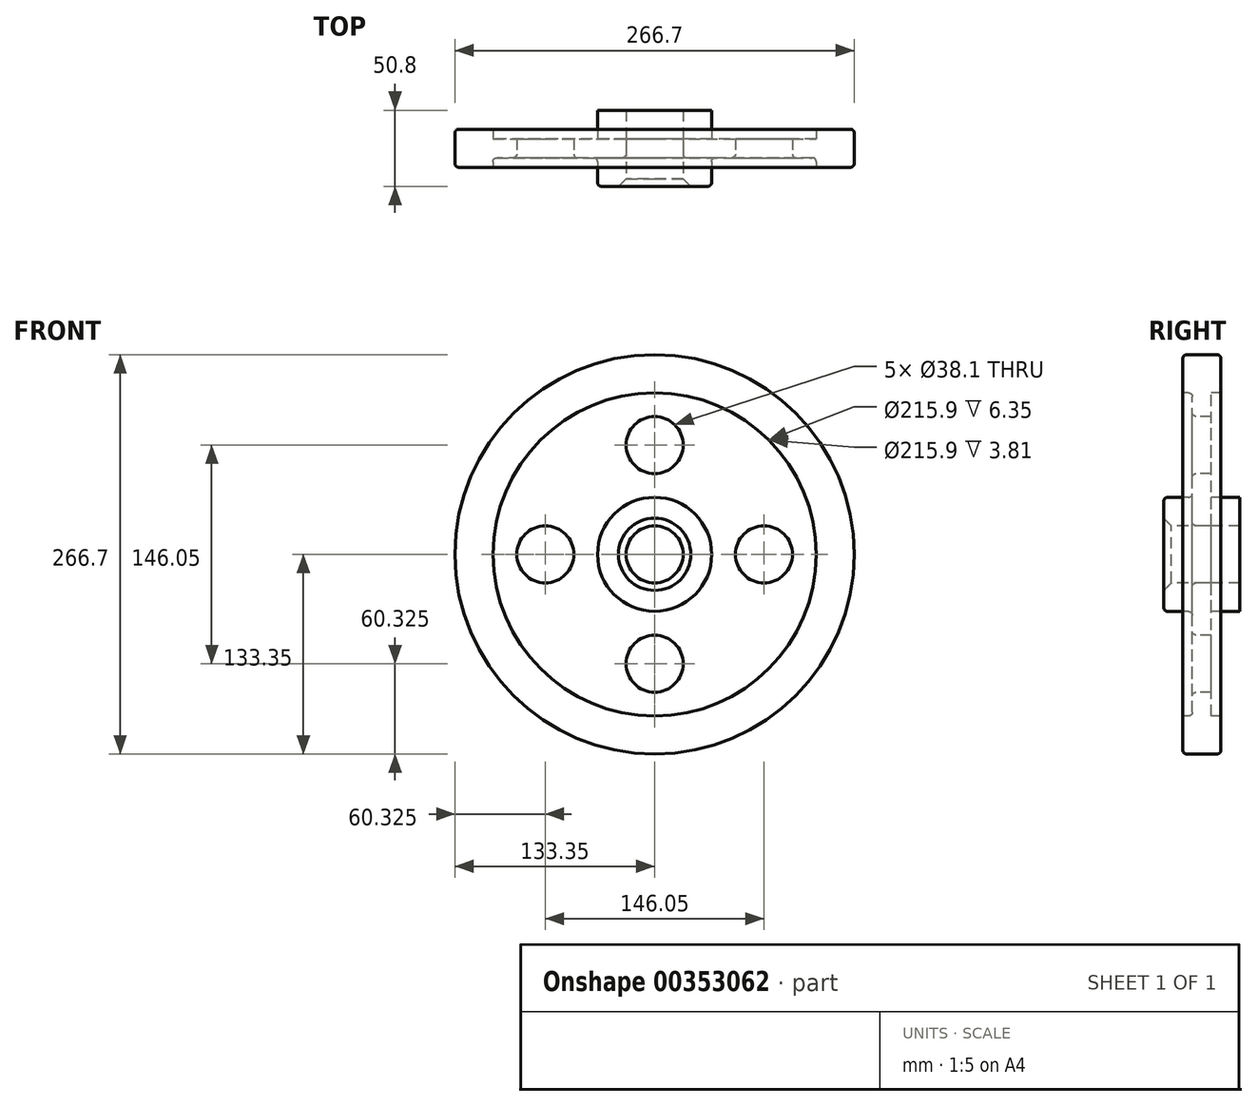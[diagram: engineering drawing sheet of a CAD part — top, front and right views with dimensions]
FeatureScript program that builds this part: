
annotation { "Feature Type Name" : "Feature", "Feature Type Description" : "" }
export const myFeature = defineFeature(function(context is Context, id is Id, definition is map)
    precondition{}
    {
        {
            var Q0;
            Q0=qCreatedBy(makeId("Right.planeOp"),FACE);
            var sketch = newSketch(context, id + "F0", { "sketchPlane" : qUnion([Q0])});
            skLineSegment(sketch, "E0", {"start": v(0, 0) * mm, "end": v(216.84, 0) * mm, "construction": true});
            skLineSegment(sketch, "E1", {"start": v(0, 0) * mm, "end": v(0, 371.48) * mm, "construction": true});
            skLineSegment(sketch, "E2.0", {"start": v(6.35, 38.1) * mm, "end": v(6.35, 107.95) * mm});
            skLineSegment(sketch, "E3.0", {"start": v(25.4, 19.05) * mm, "end": v(25.4, 38.1) * mm});
            skLineSegment(sketch, "E4.0", {"start": v(0, 19.05) * mm, "end": v(25.4, 19.05) * mm});
            skLineSegment(sketch, "E5.0", {"start": v(6.35, 38.1) * mm, "end": v(25.4, 38.1) * mm});
            skLineSegment(sketch, "E6.0", {"start": v(6.35, 107.95) * mm, "end": v(12.7, 107.95) * mm});
            skLineSegment(sketch, "E7.0", {"start": v(0, 133.35) * mm, "end": v(12.7, 133.35) * mm});
            skLineSegment(sketch, "E8.trimOffspring", {"start": v(12.7, 107.95) * mm, "end": v(12.7, 133.35) * mm});
            skLineSegment(sketch, "E9.MirrorCS", {"start": v(0, 133.35) * mm, "end": v(-12.7, 133.35) * mm});
            skLineSegment(sketch, "E10.MirrorCS", {"start": v(-12.7, 107.95) * mm, "end": v(-12.7, 133.35) * mm});
            skLineSegment(sketch, "E11.MirrorCS", {"start": v(-6.35, 38.1) * mm, "end": v(-6.35, 107.95) * mm});
            skLineSegment(sketch, "E12.MirrorCS", {"start": v(-6.35, 107.95) * mm, "end": v(-12.7, 107.95) * mm});
            skLineSegment(sketch, "E13.MirrorCS", {"start": v(-6.35, 38.1) * mm, "end": v(-25.4, 38.1) * mm});
            skLineSegment(sketch, "E14.MirrorCS", {"start": v(-25.4, 19.05) * mm, "end": v(-25.4, 38.1) * mm});
            skLineSegment(sketch, "E15.MirrorCS", {"start": v(0, 19.05) * mm, "end": v(-25.4, 19.05) * mm});
            skLineSegment(sketch, "E16.MirrorCS", {"start": v(0, 0) * mm, "end": v(-216.84, 0) * mm, "construction": true});
            skSolve(sketch);
        }
        {
            var Q0;
            Q0=makeQuery(id+"F0.imprint","IMPRINT",FACE,{"disambiguationData":[TD([[makeQuery(id+"F0.imprint","IMPRINT",EDGE,{"derivedFrom":sQuery(id+"F0.wireOp",EDGE,"E2.0")}),1.0]])]});
            var Q1;
            Q1=sQuery(id+"F0.wireOp",EDGE,"E0");
            revolve(context, id + "F1", {"entities" : qUnion([Q0]), "axis" : qUnion([Q1]), "revolveType" : RevolveType.FULL});
        }
        {
            var Q0;
            Q0=makeQuery(id+"F1.opRevolve","SWEPT_FACE",FACE,{"disambiguationData":[OSD([sQuery(id+"F0.wireOp",EDGE,"E11.MirrorCS")])]});
            var sketch = newSketch(context, id + "F2", { "sketchPlane" : qUnion([Q0])});
            skLineSegment(sketch, "E17", {"start": v(0, 0) * mm, "end": v(0, 73.03) * mm});
            skCircle(sketch, "E18", {"center": v(0, 73.03) * mm, "radius": 19.05 * mm});
            skCircle(sketch, "E19.1.0", {"center": v(-73.03, 0) * mm, "radius": 19.05 * mm});
            skCircle(sketch, "E19.2.0", {"center": v(0, -73.03) * mm, "radius": 19.05 * mm});
            skCircle(sketch, "E19.3.0", {"center": v(73.03, 0) * mm, "radius": 19.05 * mm});
            skPoint(sketch, "E19.center", {"position": v(0, 0) * mm});
            skSolve(sketch);
        }
        {
            var Q0;
            Q0 = qSketchRegion(id + "F2", true);
            extrude(context, id + "F3", {"entities" : qUnion([Q0]), "operationType" : NewBodyOperationType.REMOVE, "oppositeDirection" : true, "depth" : 25.4 * mm});
        }
        {
            var Q0;
            Q0=makeQuery(id+"F1.opRevolve","SWEPT_FACE",FACE,{"disambiguationData":[OSD([sQuery(id+"F0.wireOp",EDGE,"E11.MirrorCS")])]});
            var Q1;
            Q1=makeQuery(id+"F1.opRevolve","SWEPT_EDGE",EDGE,{"disambiguationData":[OSD([sQuery(id+"F0.wireOp",EDGE,"E14.MirrorCS"),sQuery(id+"F0.wireOp",EDGE,"E13.MirrorCS")])]});
            var Q2;
            Q2=makeQuery(id+"F1.opRevolve","SWEPT_EDGE",EDGE,{"disambiguationData":[OSD([sQuery(id+"F0.wireOp",EDGE,"E9.MirrorCS"),sQuery(id+"F0.wireOp",EDGE,"E10.MirrorCS")])]});
            var Q3;
            Q3=makeQuery(id+"F1.opRevolve","SWEPT_EDGE",EDGE,{"disambiguationData":[OSD([sQuery(id+"F0.wireOp",EDGE,"E11.MirrorCS"),sQuery(id+"F0.wireOp",EDGE,"E13.MirrorCS")])]});
            var Q4;
            Q4=makeQuery(id+"F1.opRevolve","SWEPT_EDGE",EDGE,{"disambiguationData":[OSD([sQuery(id+"F0.wireOp",EDGE,"E7.0"),sQuery(id+"F0.wireOp",EDGE,"E8.trimOffspring")])]});
            fillet(context, id + "F4", {"entities" : qUnion([Q0, Q1, Q2, Q3, Q4]), "radius" : 2.54 * mm, "tangentPropagation" : true, "allowEdgeOverflow" : false});
        }
        {
            var Q0;
            Q0=makeQuery(id+"F1.opRevolve","SWEPT_EDGE",EDGE,{"disambiguationData":[OSD([sQuery(id+"F0.wireOp",EDGE,"E14.MirrorCS"),sQuery(id+"F0.wireOp",EDGE,"E15.MirrorCS")])]});
            chamfer(context, id + "F5", {"entities" : qUnion([Q0]), "width" : 5.08 * mm, "tangentPropagation" : true});
        }
    });
